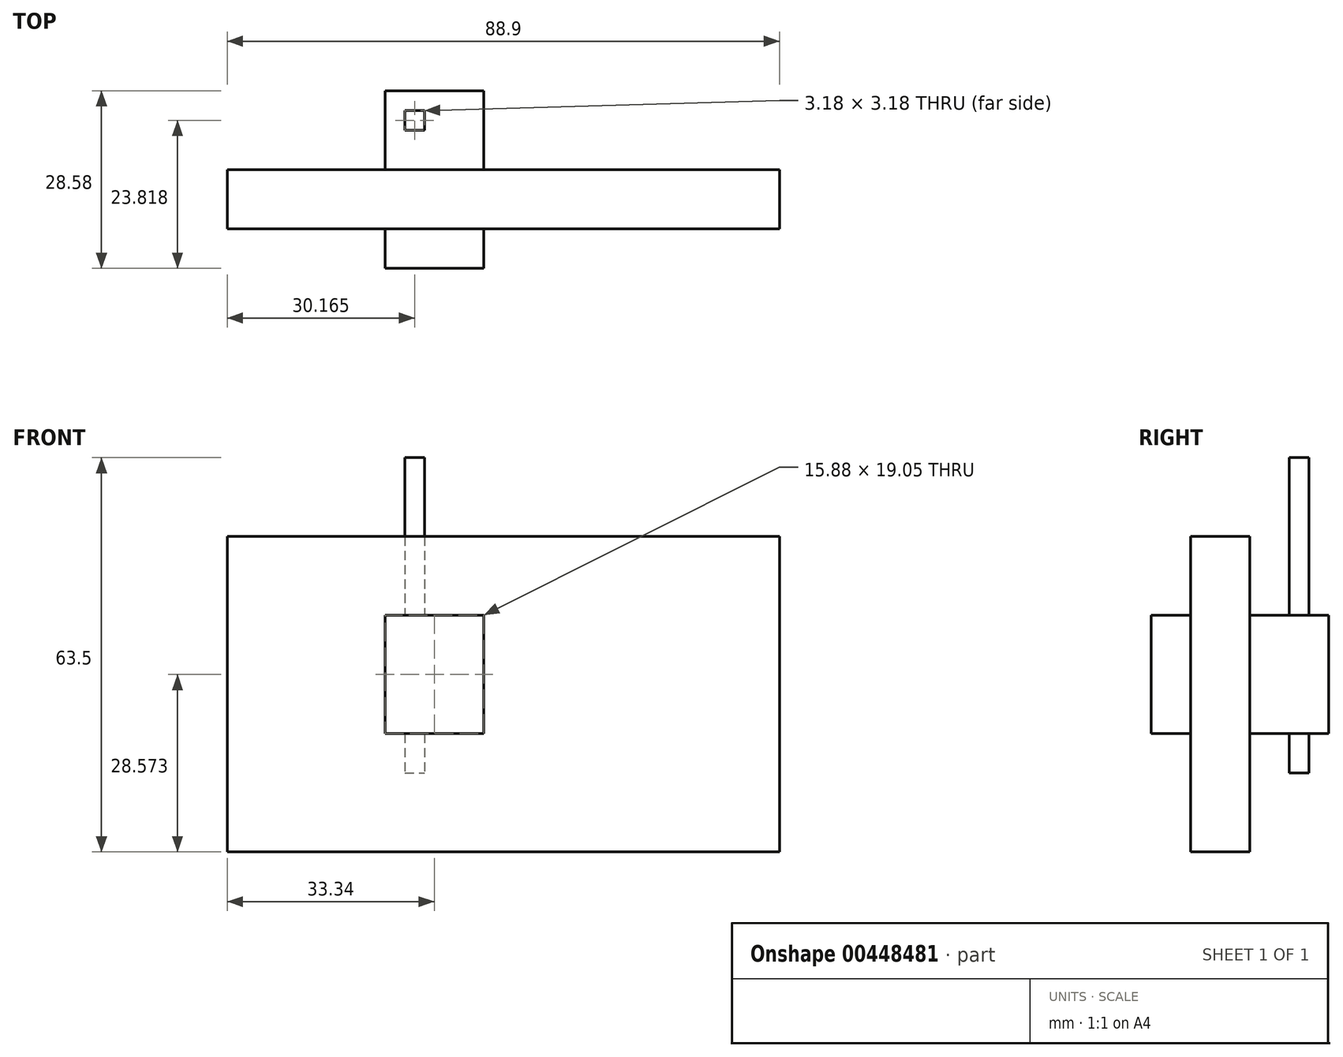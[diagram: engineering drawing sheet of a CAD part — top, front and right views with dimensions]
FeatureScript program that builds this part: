
annotation { "Feature Type Name" : "Feature", "Feature Type Description" : "" }
export const myFeature = defineFeature(function(context is Context, id is Id, definition is map)
    precondition{}
    {
        {
            var Q0;
            Q0=qCreatedBy(makeId("Front.planeOp"),FACE);
            var sketch = newSketch(context, id + "F0", { "sketchPlane" : qUnion([Q0])});
            skLineSegment(sketch, "E0.bottom", {"start": v(-43, -25.33) * mm, "end": v(45.9, -25.33) * mm});
            skLineSegment(sketch, "E0.top", {"start": v(-43, 25.47) * mm, "end": v(45.9, 25.47) * mm});
            skLineSegment(sketch, "E0.left", {"start": v(-43, -25.33) * mm, "end": v(-43, 25.47) * mm});
            skLineSegment(sketch, "E0.right", {"start": v(45.9, -25.33) * mm, "end": v(45.9, 25.47) * mm});
            skSolve(sketch);
        }
        {
            var Q0;
            Q0=makeQuery(id+"F0.imprint","IMPRINT",FACE,{"disambiguationData":[TD([[makeQuery(id+"F0.imprint","IMPRINT",EDGE,{"derivedFrom":sQuery(id+"F0.wireOp",EDGE,"E0.bottom")}),1.0]])]});
            extrude(context, id + "F1", {"entities" : qUnion([Q0]), "depth" : 9.52 * mm});
        }
        {
            var Q0;
            Q0=makeQuery(id+"F1.opExtrude","CAP_FACE",FACE,{"disambiguationData":[OSD([sQuery(id+"F0.wireOp",EDGE,"E0.bottom"),sQuery(id+"F0.wireOp",EDGE,"E0.top"),sQuery(id+"F0.wireOp",EDGE,"E0.left"),sQuery(id+"F0.wireOp",EDGE,"E0.right")])],"isStart":false});
            var sketch = newSketch(context, id + "F2", { "sketchPlane" : qUnion([Q0])});
            skLineSegment(sketch, "E1.bottom", {"start": v(-17.6, 12.77) * mm, "end": v(-1.72, 12.77) * mm});
            skLineSegment(sketch, "E1.top", {"start": v(-17.6, -6.28) * mm, "end": v(-1.72, -6.28) * mm});
            skLineSegment(sketch, "E1.left", {"start": v(-17.6, 12.77) * mm, "end": v(-17.6, -6.28) * mm});
            skLineSegment(sketch, "E1.right", {"start": v(-1.72, 12.77) * mm, "end": v(-1.72, -6.28) * mm});
            skSolve(sketch);
        }
        {
            var Q0;
            Q0=makeQuery(id+"F2.imprint","IMPRINT",FACE,{"disambiguationData":[TD([[makeQuery(id+"F2.imprint","IMPRINT",EDGE,{"derivedFrom":sQuery(id+"F2.wireOp",EDGE,"E1.bottom")}),-1.0]])]});
            extrude(context, id + "F3", {"entities" : qUnion([Q0]), "operationType" : NewBodyOperationType.ADD, "depth" : 6.35 * mm, "hasSecondDirection" : true, "secondDirectionOppositeDirection" : true, "secondDirectionDepth" : 22.22 * mm});
        }
        {
            var Q0;
            {var subQ2=sQuery(id+"F2.wireOp",EDGE,"E1.bottom");Q0=makeQuery(id+"F3.boolean.opBoolean","SPLIT",FACE,{"disambiguationData":[TD([makeQuery(id+"F1.opExtrude","CAP_FACE",FACE,{"disambiguationData":[OSD([sQuery(id+"F0.wireOp",EDGE,"E0.bottom"),sQuery(id+"F0.wireOp",EDGE,"E0.top"),sQuery(id+"F0.wireOp",EDGE,"E0.left"),sQuery(id+"F0.wireOp",EDGE,"E0.right")])],"isStart":true})])],"derivedFrom":makeQuery(id+"F3.opExtrude","SWEPT_FACE",FACE,{"disambiguationData":[OSD([subQ2])]})});}
            var sketch = newSketch(context, id + "F4", { "sketchPlane" : qUnion([Q0])});
            skLineSegment(sketch, "E2.bottom", {"start": v(-14.42, 9.53) * mm, "end": v(-11.25, 9.53) * mm});
            skLineSegment(sketch, "E2.top", {"start": v(-14.42, 6.35) * mm, "end": v(-11.25, 6.35) * mm});
            skLineSegment(sketch, "E2.left", {"start": v(-14.42, 9.53) * mm, "end": v(-14.42, 6.35) * mm});
            skLineSegment(sketch, "E2.right", {"start": v(-11.25, 9.53) * mm, "end": v(-11.25, 6.35) * mm});
            skSolve(sketch);
        }
        {
            var Q0;
            Q0=makeQuery(id+"F4.imprint","IMPRINT",FACE,{"disambiguationData":[TD([[makeQuery(id+"F4.imprint","IMPRINT",EDGE,{"derivedFrom":sQuery(id+"F4.wireOp",EDGE,"E2.bottom")}),-1.0]])]});
            extrude(context, id + "F5", {"entities" : qUnion([Q0]), "operationType" : NewBodyOperationType.ADD, "depth" : 25.4 * mm, "hasSecondDirection" : true, "secondDirectionOppositeDirection" : true, "secondDirectionDepth" : 25.4 * mm});
        }
    });
